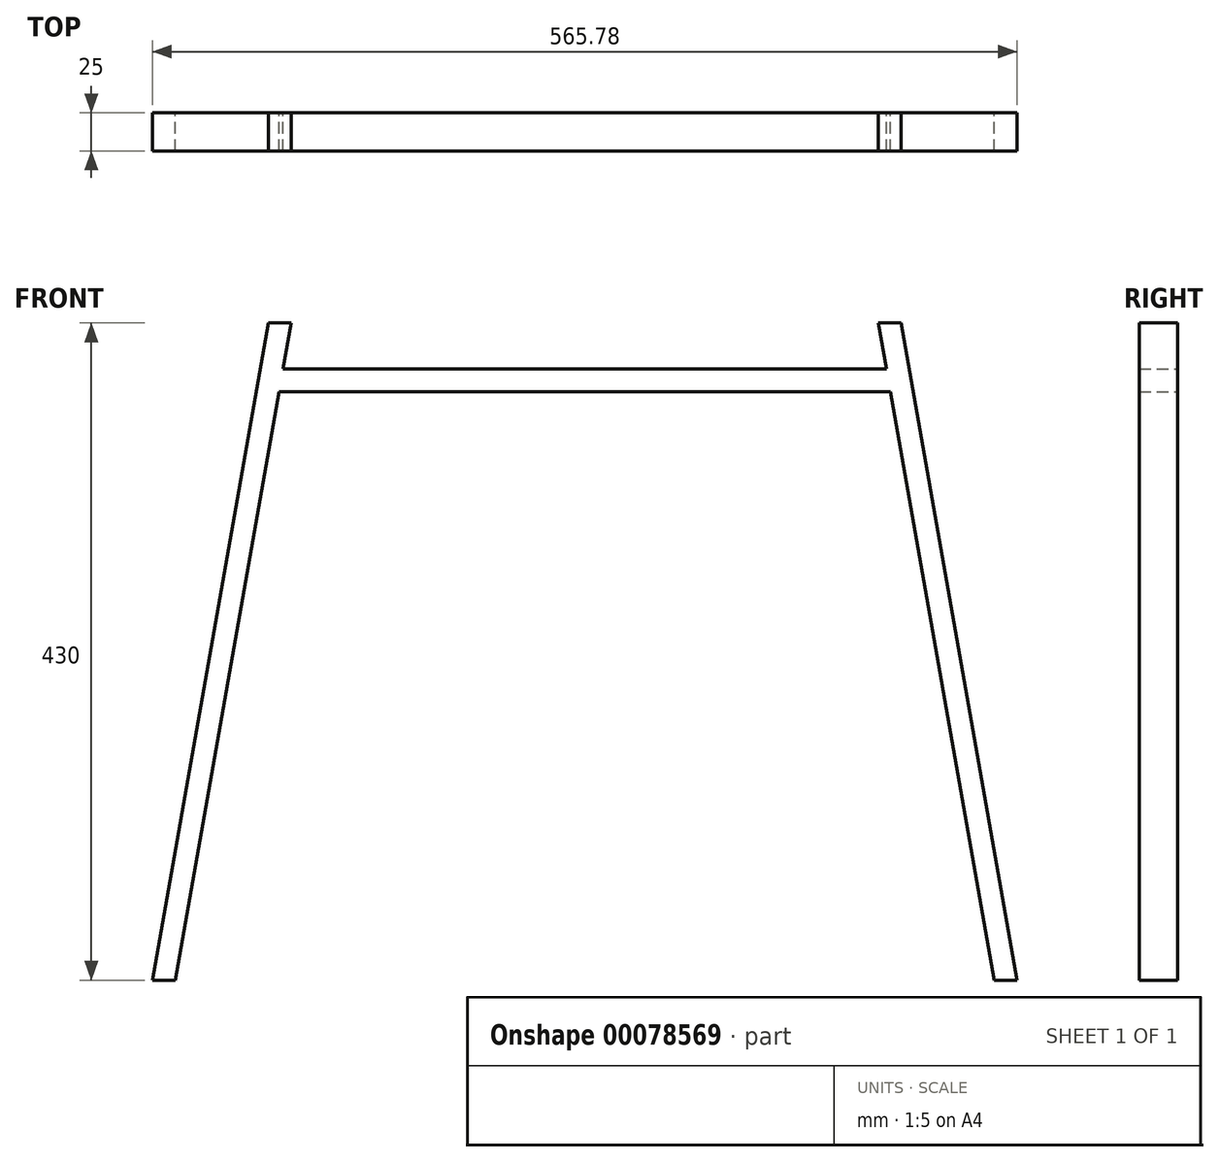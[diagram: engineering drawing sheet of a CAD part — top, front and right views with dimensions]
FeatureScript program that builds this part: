
annotation { "Feature Type Name" : "Feature", "Feature Type Description" : "" }
export const myFeature = defineFeature(function(context is Context, id is Id, definition is map)
    precondition{}
    {
        {
            var Q0;
            Q0=qCreatedBy(makeId("Front.planeOp"),FACE);
            var sketch = newSketch(context, id + "F0", { "sketchPlane" : qUnion([Q0])});
            skLineSegment(sketch, "E0", {"start": v(-282.89, 0) * mm, "end": v(-207.07, 430) * mm});
            skLineSegment(sketch, "E1", {"start": v(-207.07, 430) * mm, "end": v(-192.07, 430) * mm});
            skLineSegment(sketch, "E2", {"start": v(-192.07, 430) * mm, "end": v(-197.36, 400) * mm});
            skLineSegment(sketch, "E3", {"start": v(-197.36, 400) * mm, "end": v(0, 400) * mm});
            skLineSegment(sketch, "E4", {"start": v(0, 400) * mm, "end": v(0, 385) * mm});
            skLineSegment(sketch, "E5", {"start": v(0, 385) * mm, "end": v(-200, 385) * mm});
            skLineSegment(sketch, "E6", {"start": v(-200, 385) * mm, "end": v(-267.89, 0) * mm});
            skLineSegment(sketch, "E7", {"start": v(-267.89, 0) * mm, "end": v(-282.89, 0) * mm});
            skLineSegment(sketch, "E8.MirrorCS", {"start": v(267.89, 0) * mm, "end": v(282.89, 0) * mm});
            skLineSegment(sketch, "E9.MirrorCS", {"start": v(207.07, 430) * mm, "end": v(192.07, 430) * mm});
            skLineSegment(sketch, "E10.MirrorCS", {"start": v(0, 385) * mm, "end": v(200, 385) * mm});
            skLineSegment(sketch, "E11.MirrorCS", {"start": v(200, 385) * mm, "end": v(267.89, 0) * mm});
            skLineSegment(sketch, "E12.MirrorCS", {"start": v(192.07, 430) * mm, "end": v(197.36, 400) * mm});
            skLineSegment(sketch, "E13.MirrorCS", {"start": v(197.36, 400) * mm, "end": v(0, 400) * mm});
            skLineSegment(sketch, "E14.MirrorCS", {"start": v(282.89, 0) * mm, "end": v(207.07, 430) * mm});
            skSolve(sketch);
        }
        {
            var Q0;
            Q0=makeQuery(id+"F0.imprint","IMPRINT",FACE,{"disambiguationData":[TD([[makeQuery(id+"F0.imprint","IMPRINT",EDGE,{"derivedFrom":sQuery(id+"F0.wireOp",EDGE,"E8.MirrorCS")}),1.0]])]});
            var Q1;
            Q1=makeQuery(id+"F0.imprint","IMPRINT",FACE,{"disambiguationData":[TD([[makeQuery(id+"F0.imprint","IMPRINT",EDGE,{"derivedFrom":sQuery(id+"F0.wireOp",EDGE,"E0")}),-1.0]])]});
            extrude(context, id + "F1", {"entities" : qUnion([Q0, Q1]), "depth" : 25 * mm});
        }
        {
            var Q0;
            Q0=makeQuery(id+"F1.opExtrude","CAP_FACE",FACE,{"disambiguationData":[OSD([sQuery(id+"F0.wireOp",EDGE,"E0"),sQuery(id+"F0.wireOp",EDGE,"E1"),sQuery(id+"F0.wireOp",EDGE,"E2"),sQuery(id+"F0.wireOp",EDGE,"E3"),sQuery(id+"F0.wireOp",EDGE,"E5"),sQuery(id+"F0.wireOp",EDGE,"E6"),sQuery(id+"F0.wireOp",EDGE,"E7"),sQuery(id+"F0.wireOp",EDGE,"E8.MirrorCS"),sQuery(id+"F0.wireOp",EDGE,"E9.MirrorCS"),sQuery(id+"F0.wireOp",EDGE,"E10.MirrorCS"),sQuery(id+"F0.wireOp",EDGE,"E11.MirrorCS"),sQuery(id+"F0.wireOp",EDGE,"E12.MirrorCS"),sQuery(id+"F0.wireOp",EDGE,"E13.MirrorCS"),sQuery(id+"F0.wireOp",EDGE,"E14.MirrorCS")])],"isStart":false});
            var sketch = newSketch(context, id + "F2", { "sketchPlane" : qUnion([Q0])});
            skLineSegment(sketch, "E15", {"start": v(0, 0) * mm, "end": v(0, 593.21) * mm, "construction": true});
            skLineSegment(sketch, "E16.bottom", {"start": v(-12.5, 400) * mm, "end": v(12.5, 400) * mm});
            skLineSegment(sketch, "E16.top", {"start": v(-12.5, 392.5) * mm, "end": v(12.5, 392.5) * mm});
            skLineSegment(sketch, "E16.left", {"start": v(-12.5, 400) * mm, "end": v(-12.5, 392.5) * mm});
            skLineSegment(sketch, "E16.right", {"start": v(12.5, 400) * mm, "end": v(12.5, 392.5) * mm});
            skSolve(sketch);
        }
    });
